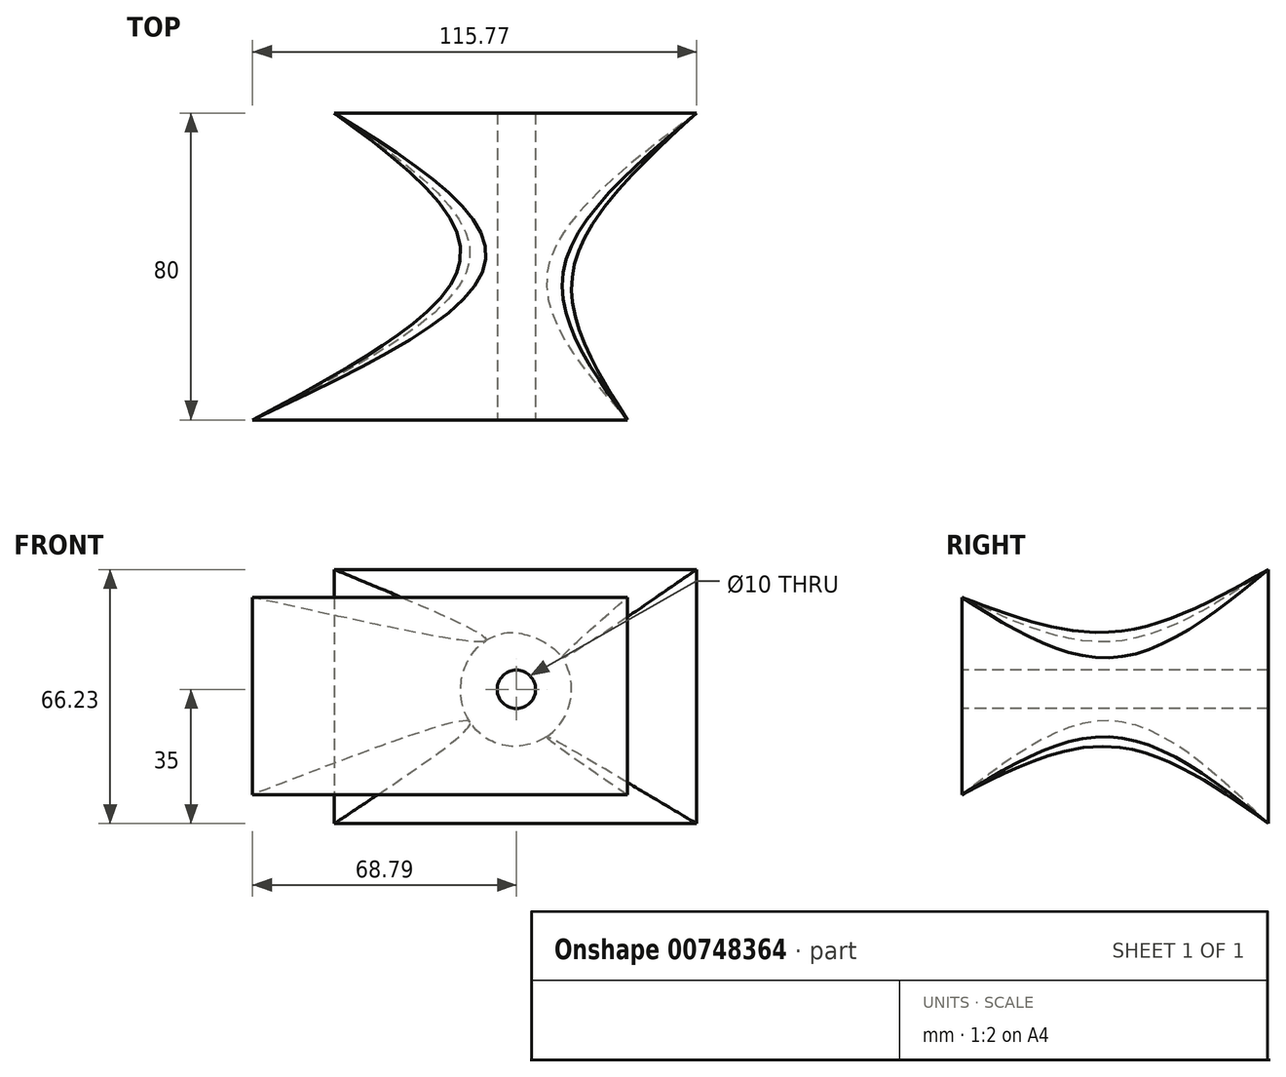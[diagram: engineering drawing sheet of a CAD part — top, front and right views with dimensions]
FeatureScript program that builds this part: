
annotation { "Feature Type Name" : "Feature", "Feature Type Description" : "" }
export const myFeature = defineFeature(function(context is Context, id is Id, definition is map)
    precondition{}
    {
        {
            var Q0;
            Q0=qCreatedBy(makeId("Front.planeOp"),FACE);
            cPlane(context, id + "F0", {"entities" : qUnion([Q0]), "cplaneType" : CPlaneType.OFFSET, "offset" : 40 * mm, "width" : 150 * mm, "height" : 150 * mm});
        }
        {
            var Q0;
            Q0=qCreatedBy(makeId("Front.planeOp"),FACE);
            cPlane(context, id + "F1", {"entities" : qUnion([Q0]), "cplaneType" : CPlaneType.OFFSET, "offset" : 40 * mm, "oppositeDirection" : true, "width" : 150 * mm, "height" : 150 * mm});
        }
        {
            var Q0;
            Q0=qCreatedBy(id+"F1.planeOp",FACE);
            var sketch = newSketch(context, id + "F2", { "sketchPlane" : qUnion([Q0])});
            skLineSegment(sketch, "E0.bottom", {"start": v(46.98, 31.23) * mm, "end": v(-47.52, 31.23) * mm});
            skLineSegment(sketch, "E0.top", {"start": v(46.98, -35) * mm, "end": v(-47.52, -35) * mm});
            skLineSegment(sketch, "E0.left", {"start": v(46.98, 31.23) * mm, "end": v(46.98, -35) * mm});
            skLineSegment(sketch, "E0.right", {"start": v(-47.52, 31.23) * mm, "end": v(-47.52, -35) * mm});
            skSolve(sketch);
        }
        {
            var Q0;
            Q0=qCreatedBy(makeId("Front.planeOp"),FACE);
            var sketch = newSketch(context, id + "F3", { "sketchPlane" : qUnion([Q0])});
            skCircle(sketch, "E1", {"center": v(0, 0) * mm, "radius": 15 * mm});
            skSolve(sketch);
        }
        {
            var Q0;
            Q0=qCreatedBy(id+"F0.planeOp",FACE);
            var sketch = newSketch(context, id + "F4", { "sketchPlane" : qUnion([Q0])});
            skLineSegment(sketch, "E2.bottom", {"start": v(28.94, 23.96) * mm, "end": v(-68.79, 23.96) * mm});
            skLineSegment(sketch, "E2.top", {"start": v(28.94, -27.46) * mm, "end": v(-68.79, -27.46) * mm});
            skLineSegment(sketch, "E2.left", {"start": v(28.94, 23.96) * mm, "end": v(28.94, -27.46) * mm});
            skLineSegment(sketch, "E2.right", {"start": v(-68.79, 23.96) * mm, "end": v(-68.79, -27.46) * mm});
            skSolve(sketch);
        }
        {
            var Q0;
            Q0=makeQuery(id+"F2.imprint","IMPRINT",FACE,{"disambiguationData":[TD([[makeQuery(id+"F2.imprint","IMPRINT",EDGE,{"derivedFrom":sQuery(id+"F2.wireOp",EDGE,"E0.bottom")}),1.0]])]});
            var Q1;
            Q1=makeQuery(id+"F3.imprint","IMPRINT",FACE,{"disambiguationData":[TD([[makeQuery(id+"F3.imprint","IMPRINT",EDGE,{"derivedFrom":sQuery(id+"F3.wireOp",EDGE,"E1")}),1.0]])]});
            var Q2;
            Q2=makeQuery(id+"F4.imprint","IMPRINT",FACE,{"disambiguationData":[TD([[makeQuery(id+"F4.imprint","IMPRINT",EDGE,{"derivedFrom":sQuery(id+"F4.wireOp",EDGE,"E2.bottom")}),1.0]])]});
            loft(context, id + "F5", {"sheetProfilesArray" : [{ "sheetProfileEntities" : qUnion([Q0]) }, { "sheetProfileEntities" : qUnion([Q1]) }, { "sheetProfileEntities" : qUnion([Q2]) }]});
        }
        {
            var Q0;
            Q0=qCreatedBy(id+"F0.planeOp",FACE);
            var sketch = newSketch(context, id + "F6", { "sketchPlane" : qUnion([Q0])});
            skCircle(sketch, "E3", {"center": v(0, 0) * mm, "radius": 5 * mm});
            skSolve(sketch);
        }
        {
            var Q0;
            Q0=makeQuery(id+"F6.imprint","IMPRINT",FACE,{"disambiguationData":[TD([[makeQuery(id+"F6.imprint","IMPRINT",EDGE,{"derivedFrom":sQuery(id+"F6.wireOp",EDGE,"E3")}),1.0]])]});
            extrude(context, id + "F7", {"entities" : qUnion([Q0]), "operationType" : NewBodyOperationType.REMOVE, "oppositeDirection" : true, "depth" : 200 * mm, "offsetDistance" : 25 * mm});
        }
    });
